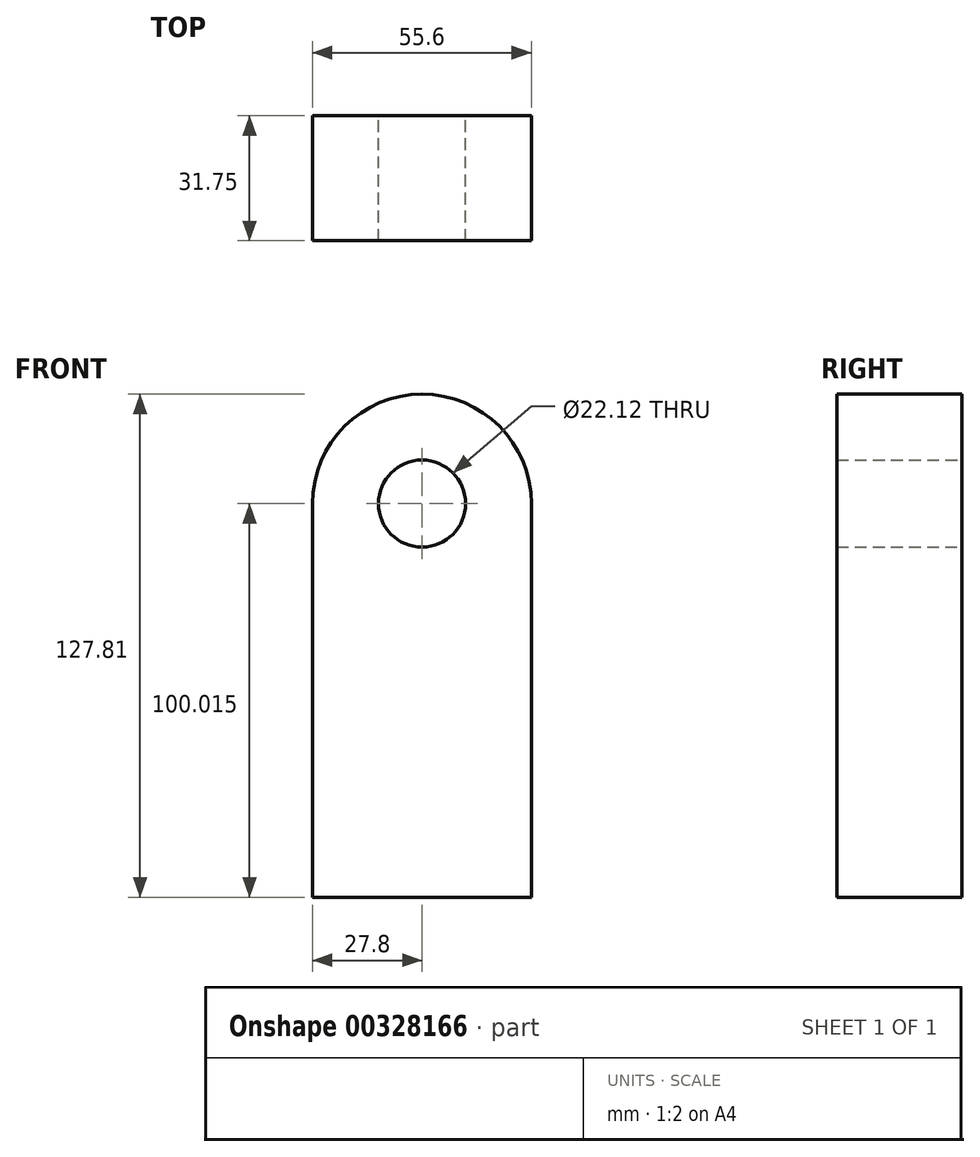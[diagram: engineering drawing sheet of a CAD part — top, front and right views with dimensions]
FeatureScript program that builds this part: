
annotation { "Feature Type Name" : "Feature", "Feature Type Description" : "" }
export const myFeature = defineFeature(function(context is Context, id is Id, definition is map)
    precondition{}
    {
        {
            var Q0;
            Q0=qCreatedBy(makeId("Front.planeOp"),FACE);
            var sketch = newSketch(context, id + "F0", { "sketchPlane" : qUnion([Q0])});
            skLineSegment(sketch, "E0.top", {"start": v(-27.8, -50) * mm, "end": v(27.8, -50) * mm});
            skLineSegment(sketch, "E0.left", {"start": v(-27.8, 50) * mm, "end": v(-27.8, -50) * mm});
            skLineSegment(sketch, "E0.right", {"start": v(27.8, 50) * mm, "end": v(27.8, -50) * mm});
            skPoint(sketch, "E0.middle", {"position": v(0, 0) * mm});
            skArc(sketch, "E1", {"start": v(27.8, 50) * mm, "mid": v(0, 77.8) * mm, "end": v(-27.8, 50) * mm});
            skCircle(sketch, "E2", {"center": v(0, 50) * mm, "radius": 11.06 * mm});
            skSolve(sketch);
        }
        {
            var Q0;
            Q0=makeQuery(id+"F0.imprint","IMPRINT",FACE,{"disambiguationData":[TD([[makeQuery(id+"F0.imprint","IMPRINT",EDGE,{"derivedFrom":sQuery(id+"F0.wireOp",EDGE,"E0.top")}),1.0]])]});
            extrude(context, id + "F1", {"entities" : qUnion([Q0]), "depth" : 31.75 * mm});
        }
    });
